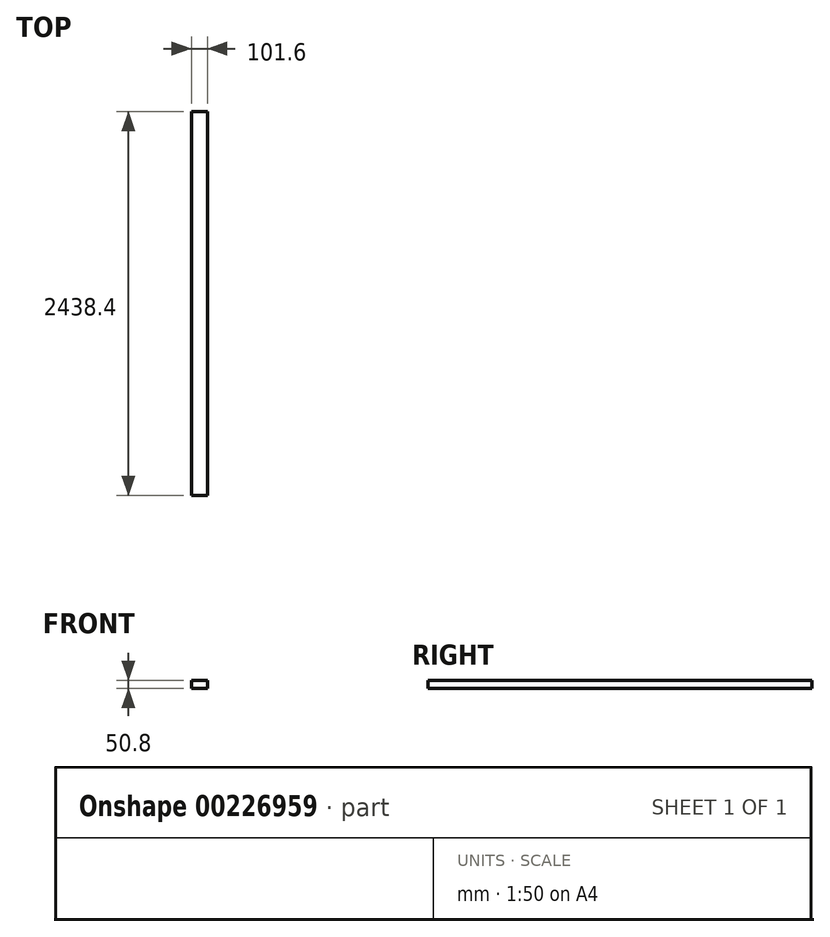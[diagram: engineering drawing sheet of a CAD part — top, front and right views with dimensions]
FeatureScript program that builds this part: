
annotation { "Feature Type Name" : "Feature", "Feature Type Description" : "" }
export const myFeature = defineFeature(function(context is Context, id is Id, definition is map)
    precondition{}
    {
        {
            var Q0;
            Q0=qCreatedBy(makeId("Front.planeOp"),FACE);
            var sketch = newSketch(context, id + "F0", { "sketchPlane" : qUnion([Q0])});
            skLineSegment(sketch, "E0.bottom", {"start": v(-60.78, 56.5) * mm, "end": v(40.82, 56.5) * mm});
            skLineSegment(sketch, "E0.top", {"start": v(-60.78, 5.7) * mm, "end": v(40.82, 5.7) * mm});
            skLineSegment(sketch, "E0.left", {"start": v(-60.78, 56.5) * mm, "end": v(-60.78, 5.7) * mm});
            skLineSegment(sketch, "E0.right", {"start": v(40.82, 56.5) * mm, "end": v(40.82, 5.7) * mm});
            skSolve(sketch);
        }
        {
            var Q0;
            Q0=makeQuery(id+"F0.imprint","IMPRINT",FACE,{"disambiguationData":[TD([[makeQuery(id+"F0.imprint","IMPRINT",EDGE,{"derivedFrom":sQuery(id+"F0.wireOp",EDGE,"E0.bottom")}),-1.0]])]});
            extrude(context, id + "F1", {"entities" : qUnion([Q0]), "depth" : 2438.4 * mm});
        }
    });
